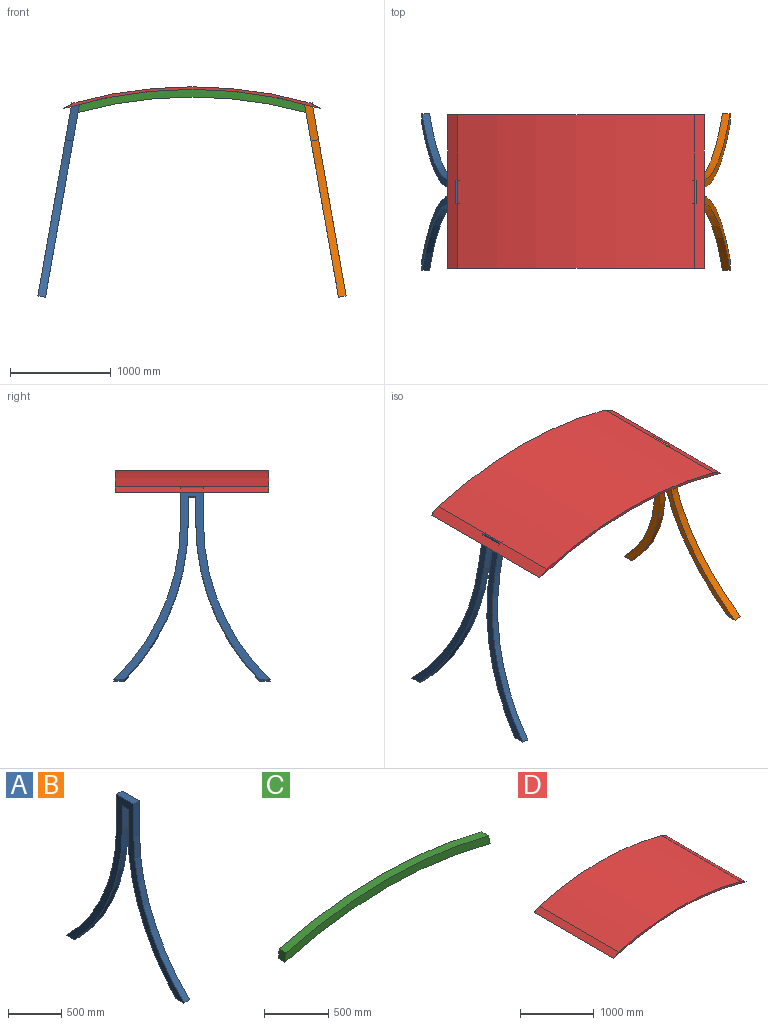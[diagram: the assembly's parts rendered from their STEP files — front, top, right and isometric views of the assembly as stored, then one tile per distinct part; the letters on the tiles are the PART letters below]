
ASSEMBLY  parts=4 mates=3
PART A: 14 faces, bbox 76.2x1554.2x1945.7 mm
  f0: plane 278.06x76.2mm, normal (0,-1,0), area 21188.3mm2, adj f1,f11,f12,f13
  f1: cylinder r=2272.71mm len=1572.39mm, axis (-1,0,0), area 132319.8mm2, adj f0,f2,f12,f13
  f2: plane 107.27x76.2mm, normal (0,0,-1), area 8174.1mm2, adj f1,f3,f12,f13
  f3: cylinder r=2196.51mm len=1572.39mm, axis (-1,0,0), area 133539.8mm2, adj f2,f4,f12,f13
  f4: plane 373.3x76.2mm, normal (0,1,0), area 28445.5mm2, adj f3,f5,f12,f13
  f5: plane 228.6x76.2mm, normal (0,0,1), area 17419.3mm2, adj f4,f6,f12,f13
  f6: plane 373.3x76.2mm, normal (0,-1,0), area 28445.5mm2, adj f5,f7,f12,f13
  f7: cylinder r=2196.51mm len=1572.39mm, axis (-1,0,0), area 133539.8mm2, adj f6,f8,f12,f13
  f8: plane 107.27x76.2mm, normal (0,0,-1), area 8174.1mm2, adj f7,f9,f12,f13
  f9: cylinder r=2272.71mm len=1572.39mm, axis (-1,0,0), area 132319.8mm2, adj f8,f10,f12,f13
  f10: plane 278.06x76.2mm, normal (0,1,0), area 21188.3mm2, adj f9,f11,f12,f13
  f11: plane 76.2x76.2mm, normal (0,0,-1), area 5806.4mm2, adj f0,f10,f12,f13
  f12: plane 1945.69x1554.21mm, normal (1,0,0), area 329975.8mm2, adj f0,f1,f2,f3,f4,f5,f6,f7
  f13: plane 1945.69x1554.21mm, normal (-1,0,0), area 329975.8mm2, adj f0,f1,f2,f3,f4,f5,f6,f7
PART B: same geometry as A
PART C: 6 faces, bbox 2260.6x76.2x228.6 mm
  f0: cylinder r=4267.73mm len=2260.6mm, axis (0,1,0), area 174337.9mm2, adj f1,f3,f4,f5
  f1: plane 82.88x76.2mm, normal (0.98,0,0.17), area 6412.9mm2, adj f0,f2,f4,f5
  f2: cylinder r=4343.93mm len=2231.37mm, axis (0,1,0), area 171957.7mm2, adj f1,f3,f4,f5
  f3: plane 82.88x76.2mm, normal (-0.98,0,0.17), area 6412.9mm2, adj f0,f2,f4,f5
  f4: plane 2260.6x228.6mm, normal (0,-1,0), area 173146mm2, adj f0,f1,f2,f3
  f5: plane 2260.6x228.6mm, normal (0,1,0), area 173146mm2, adj f0,f1,f2,f3
PART D: 6 faces, bbox 2540x1524x215.2 mm
  f0: cylinder r=4369.31mm len=2341.54mm, axis (0,1,0), area 3612649.5mm2, adj f1,f3,f4,f5
  f1: plane 1524x99.23mm, normal (-0.49,0,0.87), area 173214.5mm2, adj f0,f2,f4,f5
  f2: cylinder r=4343.91mm len=2540mm, axis (0,1,0), area 3928341.7mm2, adj f1,f3,f4,f5
  f3: plane 1524x99.23mm, normal (0.49,0,0.87), area 173214.5mm2, adj f0,f2,f4,f5
  f4: plane 2540x215.2mm, normal (0,-1,0), area 62789.6mm2, adj f0,f1,f2,f3
  f5: plane 2540x215.2mm, normal (0,1,0), area 62789.6mm2, adj f0,f1,f2,f3
PLACE A rot(axis=(0.09,0,1),180deg) t=(-1455.81,-151.56,-15.16)mm
PLACE B rot(axis=(0,-1,0),10deg) t=(808.64,-75.36,-15.16)mm
PLACE C t=(-323.59,-75.36,-4.25)mm fixed
PLACE D t=(-1593.59,648.54,34.53)mm
MATE fastened A.f13 <-> C.f3  axis (0.98,0,-0.17) through (-1439.27,-113.46,78.63)mm
MATE planar D.f0 <-> C.f2  axis (0,1,0) through (-323.59,-113.46,-4119.58)mm
MATE fastened B.f13 <-> C.f1  axis (-0.98,0,-0.17) through (792.1,-113.46,78.63)mm
